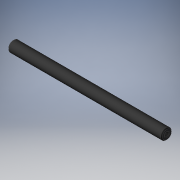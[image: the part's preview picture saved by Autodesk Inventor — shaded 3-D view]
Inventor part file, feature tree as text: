
AUTODESK INVENTOR PART (.ipt)
format: ipt  version: 2019 (Build 230136000, 136)  size: 121,856 bytes
history: native  units: mm
features: sketch x3, hole x2, revolve x1
ambient origin geometry x8: Origin, YZ Plane, XZ Plane, XY Plane, X Axis, Y Axis, Z Axis, Center Point
bodies: Solid1 (feature_tree)
feature tree (6):
  revolve  "Revolution1"  [1 undecoded]
  hole  "Hole1"  [1 undecoded]
  hole  "Hole2"  [1 undecoded]
  sketch  "Sketch_1"  dims[d0=360.0deg]
  sketch  "Sketch2"  dims[d1=2.459mm d2=6.0mm d3=3.0mm d4=2.0mm d5=90.0deg d6=6.790148mm d7=120.0deg]
  sketch  "Sketch3"  dims[d8=2.459mm d9=6.0mm d10=3.0mm d11=2.0mm d12=90.0deg d13=6.760148mm d14=120.0deg]
note: 3 required parameter values undecoded (feature->parameter linkage not recoverable at this tier; creation-order binding heuristic only, values carry confidence <= 0.55)
